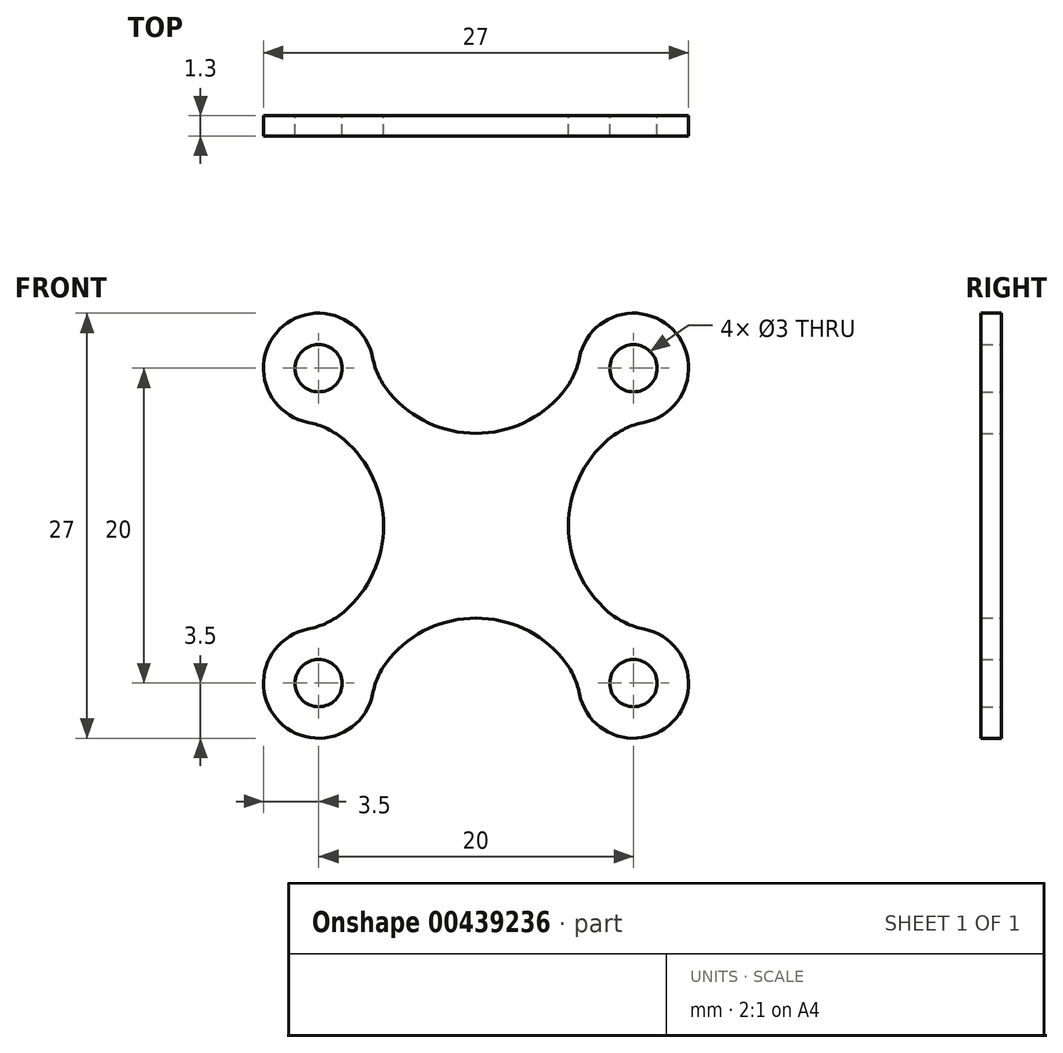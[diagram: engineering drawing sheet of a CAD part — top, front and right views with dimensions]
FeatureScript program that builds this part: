
annotation { "Feature Type Name" : "Feature", "Feature Type Description" : "" }
export const myFeature = defineFeature(function(context is Context, id is Id, definition is map)
    precondition{}
    {
        {
            var Q0;
            Q0=qCreatedBy(makeId("Front.planeOp"),FACE);
            var sketch = newSketch(context, id + "F0", { "sketchPlane" : qUnion([Q0])});
            skPoint(sketch, "E0.middle", {"position": v(0, 0) * mm});
            skCircle(sketch, "E1", {"center": v(-10, 10) * mm, "radius": 1.5 * mm});
            skCircle(sketch, "E2", {"center": v(10, 10) * mm, "radius": 1.5 * mm});
            skCircle(sketch, "E3", {"center": v(10, -10) * mm, "radius": 1.5 * mm});
            skCircle(sketch, "E4", {"center": v(-10, -10) * mm, "radius": 1.5 * mm});
            skArc(sketch, "E5.0", {"start": v(-10.67, -6.57) * mm, "mid": v(-12.47, -12.47) * mm, "end": v(-6.57, -10.67) * mm});
            skArc(sketch, "E6.0", {"start": v(-6.57, 10.67) * mm, "mid": v(-12.47, 12.47) * mm, "end": v(-10.67, 6.57) * mm});
            skArc(sketch, "E7.0", {"start": v(6.57, -10.67) * mm, "mid": v(12.47, -12.47) * mm, "end": v(10.67, -6.57) * mm});
            skArc(sketch, "E8.0", {"start": v(10.67, 6.57) * mm, "mid": v(12.47, 12.47) * mm, "end": v(6.57, 10.67) * mm});
            skArc(sketch, "E9", {"start": v(5.46, -8.4) * mm, "mid": v(0, -5.87) * mm, "end": v(-5.46, -8.4) * mm});
            skArc(sketch, "E10.MirrorCS", {"start": v(-8.4, 5.46) * mm, "mid": v(-5.87, 0) * mm, "end": v(-8.4, -5.46) * mm});
            skArc(sketch, "E11.MirrorCS", {"start": v(-5.46, 8.4) * mm, "mid": v(0, 5.87) * mm, "end": v(5.46, 8.4) * mm});
            skArc(sketch, "E12.MirrorCS", {"start": v(8.4, -5.46) * mm, "mid": v(5.87, 0) * mm, "end": v(8.4, 5.46) * mm});
            skPoint(sketch, "E13.visualSharp", {"position": v(6.5, -10) * mm});
            skArc(sketch, "E13.filletArc", {"start": v(6.57, -10.67) * mm, "mid": v(6.16, -9.46) * mm, "end": v(5.46, -8.4) * mm});
            skPoint(sketch, "E14.visualSharp", {"position": v(10, -6.5) * mm});
            skArc(sketch, "E14.filletArc", {"start": v(8.4, -5.46) * mm, "mid": v(9.46, -6.16) * mm, "end": v(10.67, -6.57) * mm});
            skPoint(sketch, "E15.visualSharp", {"position": v(-6.5, -10) * mm});
            skArc(sketch, "E15.filletArc", {"start": v(-5.46, -8.4) * mm, "mid": v(-6.16, -9.46) * mm, "end": v(-6.57, -10.67) * mm});
            skPoint(sketch, "E16.visualSharp", {"position": v(-10, -6.5) * mm});
            skArc(sketch, "E16.filletArc", {"start": v(-10.67, -6.57) * mm, "mid": v(-9.46, -6.16) * mm, "end": v(-8.4, -5.46) * mm});
            skPoint(sketch, "E17.visualSharp", {"position": v(-10, 6.5) * mm});
            skArc(sketch, "E17.filletArc", {"start": v(-8.4, 5.46) * mm, "mid": v(-9.46, 6.16) * mm, "end": v(-10.67, 6.57) * mm});
            skPoint(sketch, "E18.visualSharp", {"position": v(-6.5, 10) * mm});
            skArc(sketch, "E18.filletArc", {"start": v(-6.57, 10.67) * mm, "mid": v(-6.16, 9.46) * mm, "end": v(-5.46, 8.4) * mm});
            skPoint(sketch, "E19.visualSharp", {"position": v(10, 6.5) * mm});
            skArc(sketch, "E19.filletArc", {"start": v(10.67, 6.57) * mm, "mid": v(9.46, 6.16) * mm, "end": v(8.4, 5.46) * mm});
            skPoint(sketch, "E20.visualSharp", {"position": v(6.5, 10) * mm});
            skArc(sketch, "E20.filletArc", {"start": v(5.46, 8.4) * mm, "mid": v(6.16, 9.46) * mm, "end": v(6.57, 10.67) * mm});
            skSolve(sketch);
        }
        {
            var Q0;
            Q0=makeQuery(id+"F0.imprint","IMPRINT",FACE,{"disambiguationData":[TD([[makeQuery(id+"F0.imprint","IMPRINT",EDGE,{"derivedFrom":sQuery(id+"F0.wireOp",EDGE,"E1")}),-1.0]])]});
            extrude(context, id + "F1", {"entities" : qUnion([Q0]), "depth" : 1.3 * mm, "offsetDistance" : 25 * mm});
        }
    });
